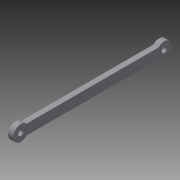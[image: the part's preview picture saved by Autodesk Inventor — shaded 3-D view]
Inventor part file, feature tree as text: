
AUTODESK INVENTOR PART (.ipt)
format: ipt  version: 2015 (Build 190159000, 159)  size: 84,992 bytes
history: native  units: in
note: dims shown in document units (in); Inventor stores cm internally (conversion verified against a paired STEP export)
features: sketch x2, extrude x1, hole x1
ambient origin geometry x8: Origin, YZ Plane, XZ Plane, XY Plane, X Axis, Y Axis, Z Axis, Center Point
bodies: Solid1 (feature_tree)
feature tree (4):
  extrude  "Extrusion1"  Depth=0.375in
  hole  "Hole1"  [1 undecoded]
  sketch  "Sketch1"  dims[d1=3.5in d2=0.375in]
  sketch  "Sketch2"  dims[d5=0.25in d6=0.375in d7=0.0in d8=0.125in d9=0.125in d10=0.0in d11=0.128in d12=0.75in d13=0.375in d14=0.25in d15=0.5635in d16=1.0in d17=0.8108in]
note: 1 required parameter value undecoded (feature->parameter linkage not recoverable at this tier; creation-order binding heuristic only, values carry confidence <= 0.55)
